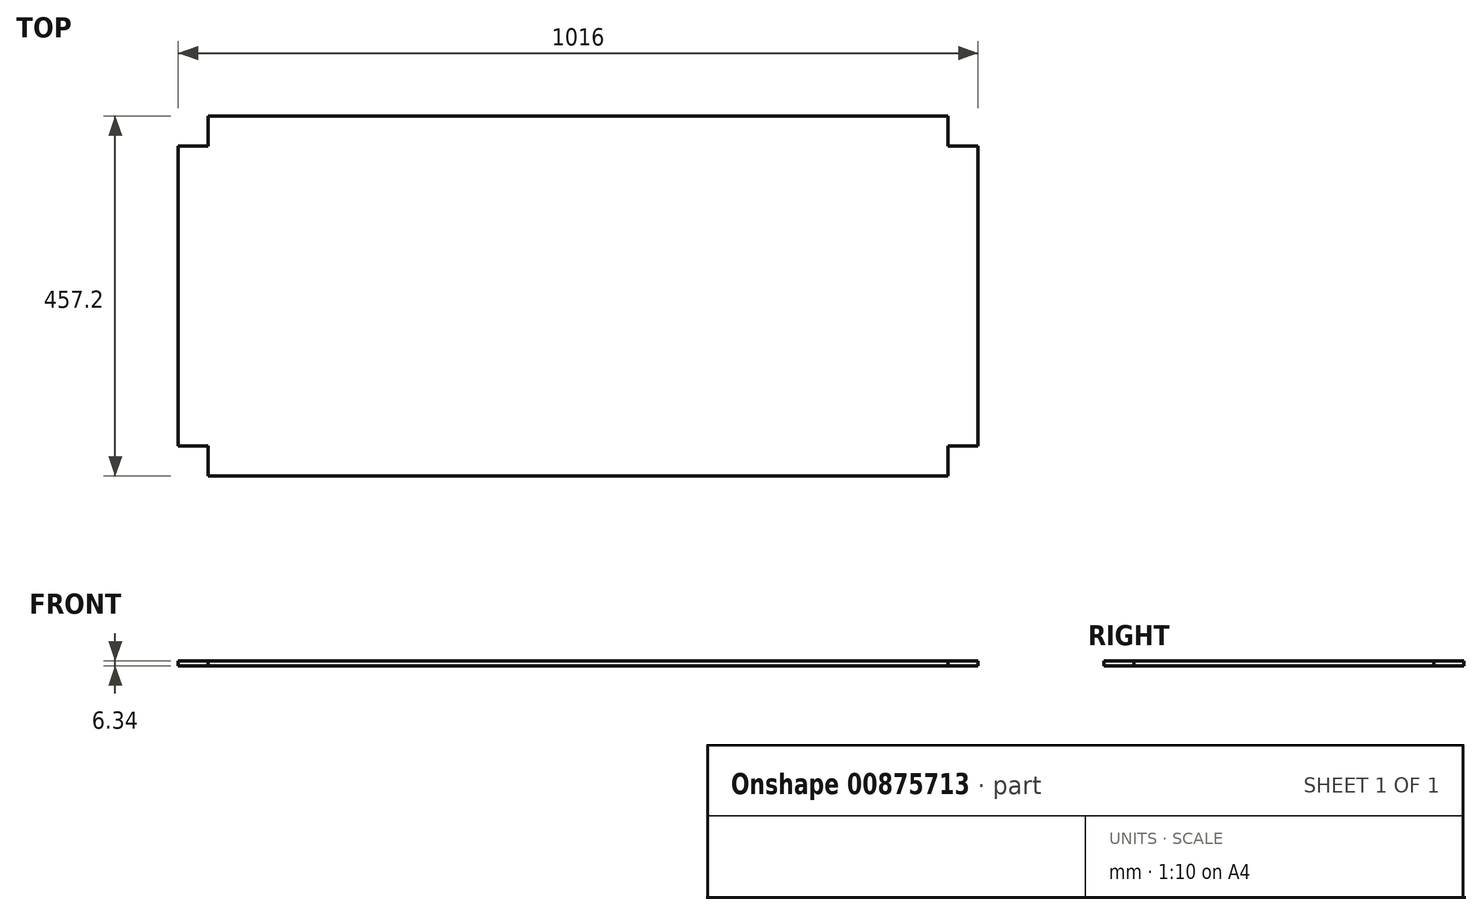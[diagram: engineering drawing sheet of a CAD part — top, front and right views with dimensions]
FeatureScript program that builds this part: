
annotation { "Feature Type Name" : "Feature", "Feature Type Description" : "" }
export const myFeature = defineFeature(function(context is Context, id is Id, definition is map)
    precondition{}
    {
        {
            var Q0;
            Q0=qCreatedBy(makeId("Top.planeOp"),FACE);
            var sketch = newSketch(context, id + "F0", { "sketchPlane" : qUnion([Q0])});
            skLineSegment(sketch, "E0.bottom", {"start": v(469.9, -228.6) * mm, "end": v(-469.9, -228.6) * mm});
            skLineSegment(sketch, "E0.top", {"start": v(469.9, 228.6) * mm, "end": v(-469.9, 228.6) * mm});
            skLineSegment(sketch, "E0.left", {"start": v(508, -190.5) * mm, "end": v(508, 190.5) * mm});
            skLineSegment(sketch, "E0.right", {"start": v(-508, -190.5) * mm, "end": v(-508, 190.5) * mm});
            skPoint(sketch, "E0.middle", {"position": v(0, 0) * mm});
            skLineSegment(sketch, "E1", {"start": v(-508, 190.5) * mm, "end": v(-469.9, 190.5) * mm});
            skLineSegment(sketch, "E2", {"start": v(-469.9, 190.5) * mm, "end": v(-469.9, 228.6) * mm});
            skPoint(sketch, "E3.orphan", {"position": v(-508, 228.6) * mm});
            skLineSegment(sketch, "E4", {"start": v(-508, -190.5) * mm, "end": v(-469.9, -190.5) * mm});
            skLineSegment(sketch, "E5", {"start": v(-469.9, -190.5) * mm, "end": v(-469.9, -228.6) * mm});
            skLineSegment(sketch, "E6", {"start": v(469.9, -228.6) * mm, "end": v(469.9, -190.5) * mm});
            skLineSegment(sketch, "E7", {"start": v(469.9, -190.5) * mm, "end": v(508, -190.5) * mm});
            skLineSegment(sketch, "E8", {"start": v(469.9, 228.6) * mm, "end": v(469.9, 190.5) * mm});
            skLineSegment(sketch, "E9", {"start": v(469.9, 190.5) * mm, "end": v(508, 190.5) * mm});
            skPoint(sketch, "E10.orphan", {"position": v(508, 228.6) * mm});
            skPoint(sketch, "E11.orphan", {"position": v(508, -228.6) * mm});
            skPoint(sketch, "E12.orphan", {"position": v(-508, -228.6) * mm});
            skSolve(sketch);
        }
        {
            var Q0;
            Q0 = qSketchRegion(id + "F0", true);
            extrude(context, id + "F1", {"entities" : qUnion([Q0]), "endBound" : BoundingType.SYMMETRIC, "depth" : 6.35 * mm, "offsetDistance" : 25.4 * mm});
        }
    });
